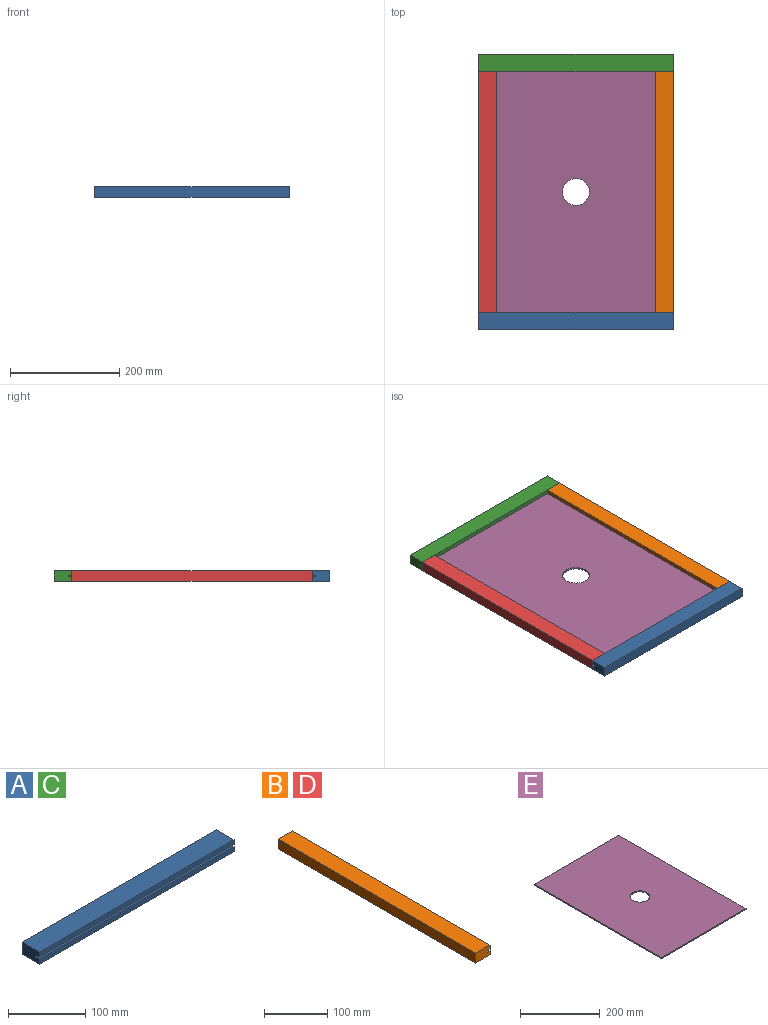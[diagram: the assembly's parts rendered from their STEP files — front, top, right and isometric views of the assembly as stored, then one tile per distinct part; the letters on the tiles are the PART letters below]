
ASSEMBLY  parts=5 mates=4
PART A: 10 faces, bbox 355.6x31.8x19.1 mm
  f0: plane 355.6x7.94mm, normal (0,-1,0), area 2822.6mm2, adj f1,f3,f4,f7
  f1: plane 31.75x19.05mm, normal (-1,0,0), area 584.7mm2, adj f0,f2,f4,f5,f6,f7,f8,f9
  f2: plane 355.6x31.75mm, normal (0,0,-1), area 11290.3mm2, adj f1,f3,f5,f6
  f3: plane 31.75x19.05mm, normal (1,0,0), area 584.7mm2, adj f0,f2,f4,f5,f6,f7,f8,f9
  f4: plane 355.6x31.75mm, normal (0,0,1), area 11290.3mm2, adj f0,f1,f3,f5
  f5: plane 355.6x19.05mm, normal (0,1,0), area 6774.2mm2, adj f1,f2,f3,f4
  f6: plane 355.6x7.94mm, normal (0,-1,0), area 2822.6mm2, adj f1,f2,f3,f8
  f7: plane 355.6x6.35mm, normal (0,0,-1), area 2258.1mm2, adj f0,f1,f3,f9
  f8: plane 355.6x6.35mm, normal (0,0,1), area 2258.1mm2, adj f1,f3,f6,f9
  f9: plane 355.6x3.18mm, normal (0,-1,0), area 1129mm2, adj f1,f3,f7,f8
PART B: 10 faces, bbox 31.8x441.3x19.1 mm
  f0: plane 441.33x19.05mm, normal (-1,0,0), area 8407.2mm2, adj f1,f7,f8,f9
  f1: plane 441.33x31.75mm, normal (0,0,-1), area 14012.1mm2, adj f0,f2,f8,f9
  f2: plane 441.33x7.94mm, normal (1,0,0), area 3503mm2, adj f1,f3,f8,f9
  f3: plane 441.33x6.35mm, normal (0,0,1), area 2802.4mm2, adj f2,f4,f8,f9
  f4: plane 441.33x3.18mm, normal (1,0,0), area 1401.2mm2, adj f3,f5,f8,f9
  f5: plane 441.33x6.35mm, normal (0,0,-1), area 2802.4mm2, adj f4,f6,f8,f9
  f6: plane 441.33x7.94mm, normal (1,0,0), area 3503mm2, adj f5,f7,f8,f9
  f7: plane 441.33x31.75mm, normal (0,0,1), area 14012.1mm2, adj f0,f6,f8,f9
  f8: plane 31.75x19.05mm, normal (0,-1,0), area 584.7mm2, adj f0,f1,f2,f3,f4,f5,f6,f7
  f9: plane 31.75x19.05mm, normal (0,1,0), area 584.7mm2, adj f0,f1,f2,f3,f4,f5,f6,f7
PART C: same geometry as A
PART D: same geometry as B
PART E: 7 faces, bbox 301.6x450.9x3.2 mm
  f0: plane 301.63x3.18mm, normal (0,-1,0), area 957.7mm2, adj f1,f4,f5,f6
  f1: plane 450.85x3.18mm, normal (1,0,0), area 1431.4mm2, adj f0,f2,f5,f6
  f2: plane 301.63x3.18mm, normal (0,1,0), area 957.7mm2, adj f1,f4,f5,f6
  f3: cylinder r=24.61mm len=49.21mm, axis (0,0,1), area 490.9mm2, adj f5,f6
  f4: plane 450.85x3.18mm, normal (-1,0,0), area 1431.4mm2, adj f0,f2,f5,f6
  f5: plane 450.85x301.63mm, normal (0,0,1), area 134085.5mm2, adj f0,f1,f2,f3,f4
  f6: plane 450.85x301.63mm, normal (0,0,-1), area 134085.5mm2, adj f0,f1,f2,f3,f4
PLACE A rot(axis=(0,0,1),180deg) t=(0,-441.33,0)mm
PLACE B rot(axis=(0,0,1),180deg) t=(-25.4,-441.33,0)mm
PLACE C at identity fixed
PLACE D t=(25.4,0,0)mm
PLACE E t=(0,-1.59,0)mm
MATE fastened D.f7 <-> C.f4  axis (0,0,1) through (-177.8,0,9.53)mm
MATE fastened C.f4 <-> B.f7  axis (0,0,1) through (177.8,0,9.53)mm
MATE fastened C.f8 <-> E.f6  axis (0,0,1) through (0,6.35,-1.59)mm
MATE fastened A.f4 <-> D.f7  axis (0,0,1) through (-177.8,-441.33,9.53)mm
